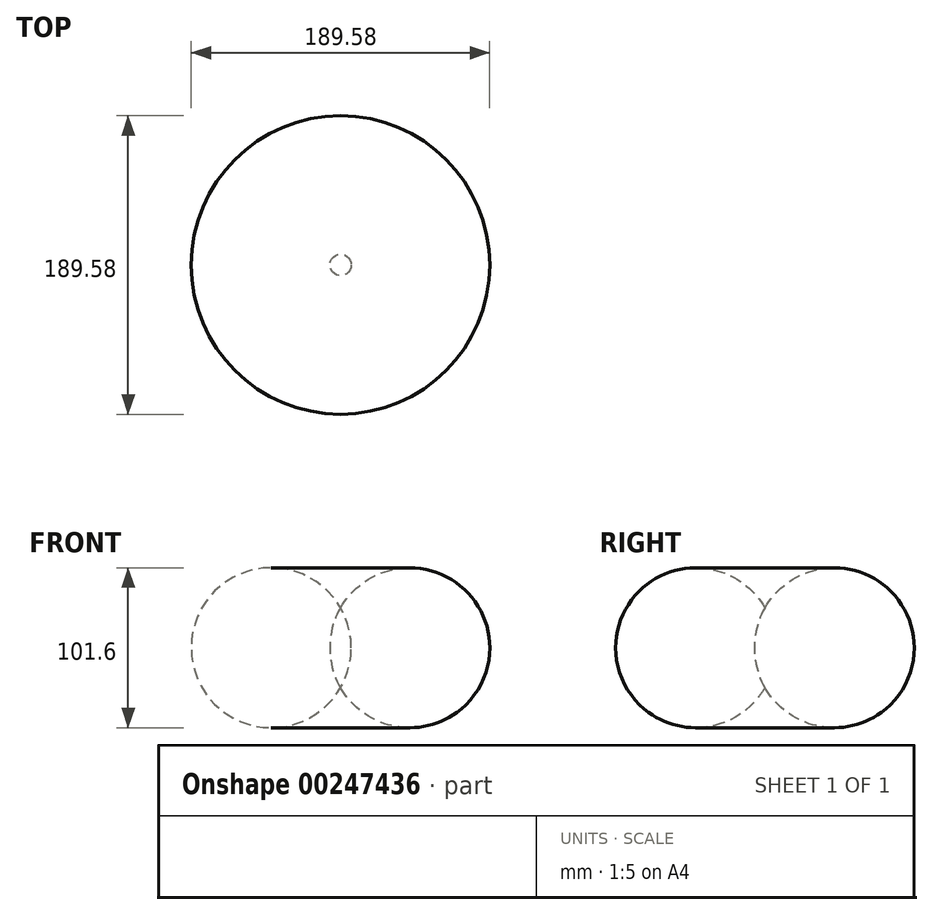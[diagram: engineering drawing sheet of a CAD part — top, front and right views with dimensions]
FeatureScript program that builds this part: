
annotation { "Feature Type Name" : "Feature", "Feature Type Description" : "" }
export const myFeature = defineFeature(function(context is Context, id is Id, definition is map)
    precondition{}
    {
        {
            var Q0;
            Q0=qCreatedBy(makeId("Front.planeOp"),FACE);
            var sketch = newSketch(context, id + "F0", { "sketchPlane" : qUnion([Q0])});
            skLineSegment(sketch, "E0", {"start": v(0, 0) * mm, "end": v(0, 50.8) * mm});
            skArc(sketch, "E1", {"start": v(0, 0) * mm, "mid": v(6.8, 25.4) * mm, "end": v(0, 50.8) * mm});
            skSolve(sketch);
        }
        {
            var Q0;
            Q0 = qSketchRegion(id + "F0", true);
            var Q1;
            Q1=sQuery(id+"F0.wireOp",EDGE,"E0");
            revolve(context, id + "F1", {"entities" : qUnion([Q0]), "axis" : qUnion([Q1]), "revolveType" : RevolveType.FULL});
        }
    });
